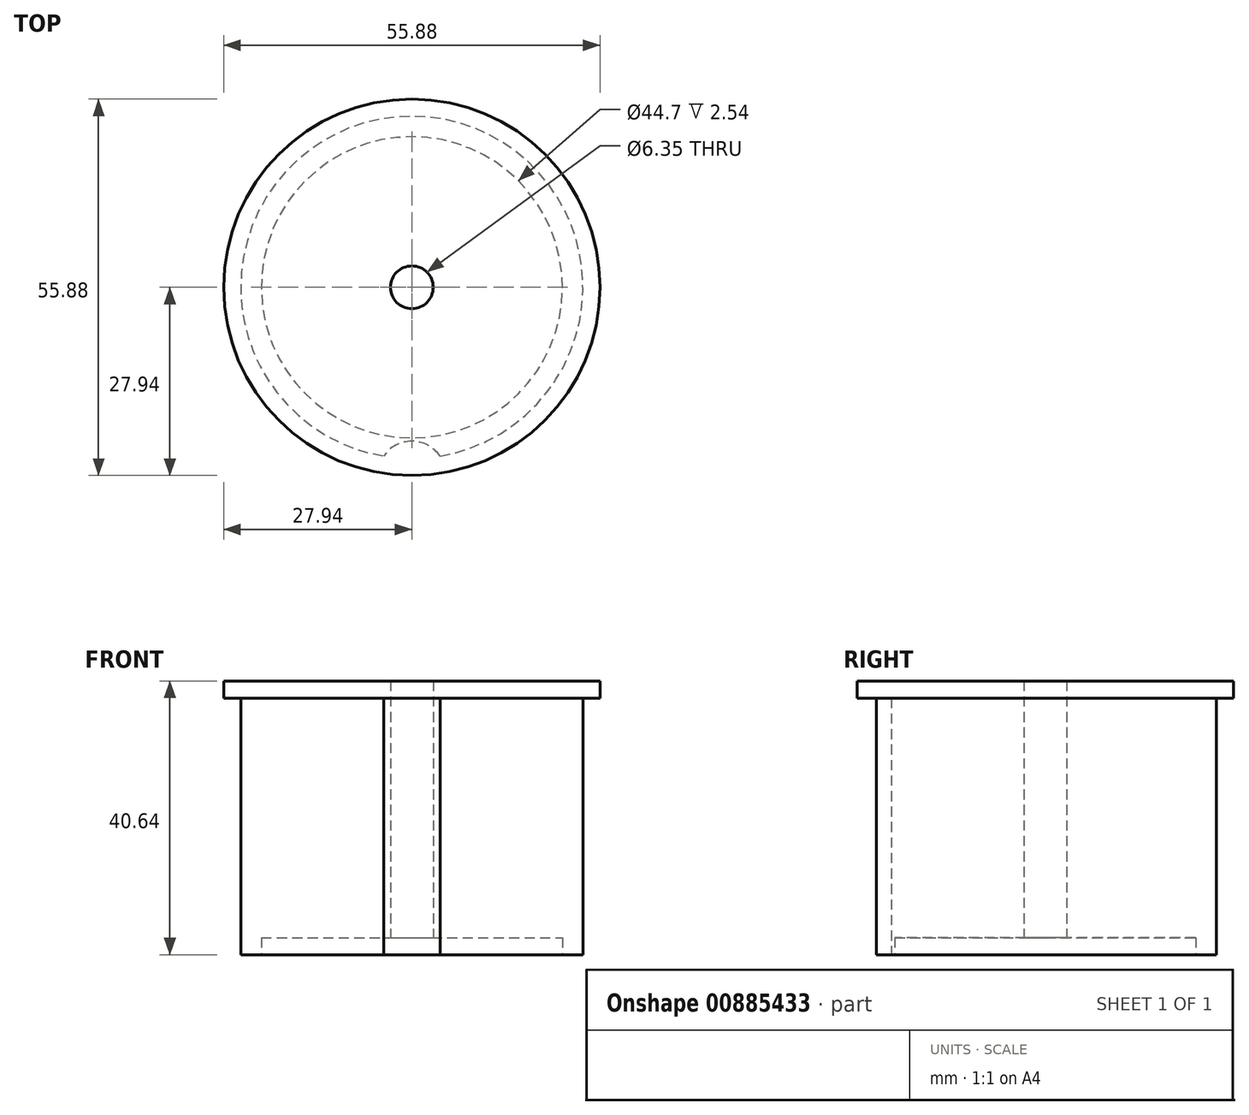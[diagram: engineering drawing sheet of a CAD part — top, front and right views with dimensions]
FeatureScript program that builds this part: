
annotation { "Feature Type Name" : "Feature", "Feature Type Description" : "" }
export const myFeature = defineFeature(function(context is Context, id is Id, definition is map)
    precondition{}
    {
        {
            var Q0;
            Q0=qCreatedBy(makeId("Top.planeOp"),FACE);
            var sketch = newSketch(context, id + "F0", { "sketchPlane" : qUnion([Q0])});
            skCircle(sketch, "E0", {"center": v(0, 0) * mm, "radius": 25.4 * mm});
            skSolve(sketch);
        }
        {
            var Q0;
            Q0 = qSketchRegion(id + "F0", true);
            extrude(context, id + "F1", {"entities" : qUnion([Q0]), "endBound" : BoundingType.SYMMETRIC, "depth" : 38.1 * mm, "offsetDistance" : 25.4 * mm});
        }
        {
            var Q0;
            Q0=makeQuery(id+"F1.opExtrude","CAP_FACE",FACE,{"disambiguationData":[OSD([sQuery(id+"F0.wireOp",EDGE,"E0")])],"isStart":false});
            var sketch = newSketch(context, id + "F2", { "sketchPlane" : qUnion([Q0])});
            skCircle(sketch, "E1", {"center": v(0, 0) * mm, "radius": 27.94 * mm});
            skSolve(sketch);
        }
        {
            var Q0;
            Q0=makeQuery(id+"F2.imprint","IMPRINT",FACE,{"disambiguationData":[TD([[makeQuery(id+"F2.imprint","IMPRINT",EDGE,{"derivedFrom":sQuery(id+"F2.wireOp",EDGE,"E1")}),1.0]])]});
            var Q1;
            Q1=makeQuery(id+"F2.imprint","IMPRINT",FACE,{"disambiguationData":[TD([[makeQuery(id+"F2.imprint","IMPRINT",EDGE,{"derivedFrom":makeQuery(id+"F1.opExtrude","CAP_EDGE",EDGE,{"disambiguationData":[OSD([sQuery(id+"F0.wireOp",EDGE,"E0")])],"isStart":false})}),1.0]])]});
            extrude(context, id + "F3", {"entities" : qUnion([Q0, Q1]), "operationType" : NewBodyOperationType.ADD, "depth" : 2.54 * mm, "offsetDistance" : 25.4 * mm});
        }
        {
            var Q0;
            Q0=makeQuery(id+"F1.opExtrude","CAP_FACE",FACE,{"disambiguationData":[OSD([sQuery(id+"F0.wireOp",EDGE,"E0")])],"isStart":true});
            var sketch = newSketch(context, id + "F4", { "sketchPlane" : qUnion([Q0])});
            skCircle(sketch, "E2", {"center": v(0, 0) * mm, "radius": 22.35 * mm});
            skSolve(sketch);
        }
        {
            var Q0;
            Q0=makeQuery(id+"F4.imprint","IMPRINT",FACE,{"disambiguationData":[TD([[makeQuery(id+"F4.imprint","IMPRINT",EDGE,{"derivedFrom":sQuery(id+"F4.wireOp",EDGE,"E2")}),1.0]])]});
            extrude(context, id + "F5", {"entities" : qUnion([Q0]), "operationType" : NewBodyOperationType.REMOVE, "oppositeDirection" : true, "depth" : 2.54 * mm, "offsetDistance" : 25.4 * mm});
        }
        {
            var Q0;
            Q0=makeQuery(id+"F5.boolean.opBoolean","COPY",FACE,{"derivedFrom":makeQuery(id+"F5.opExtrude","CAP_FACE",FACE,{"disambiguationData":[OSD([sQuery(id+"F4.wireOp",EDGE,"E2")])],"isStart":false})});
            var sketch = newSketch(context, id + "F6", { "sketchPlane" : qUnion([Q0])});
            skCircle(sketch, "E3", {"center": v(0, 0) * mm, "radius": 3.18 * mm});
            skSolve(sketch);
        }
        {
            var Q0;
            Q0=makeQuery(id+"F6.imprint","IMPRINT",FACE,{"disambiguationData":[TD([[makeQuery(id+"F6.imprint","IMPRINT",EDGE,{"derivedFrom":sQuery(id+"F6.wireOp",EDGE,"E3")}),1.0]])]});
            extrude(context, id + "F7", {"entities" : qUnion([Q0]), "operationType" : NewBodyOperationType.REMOVE, "endBound" : BoundingType.THROUGH_ALL, "oppositeDirection" : true, "depth" : 25.4 * mm, "offsetDistance" : 25.4 * mm});
        }
        {
            var Q0;
            Q0=makeQuery(id+"F1.opExtrude","CAP_FACE",FACE,{"disambiguationData":[OSD([sQuery(id+"F0.wireOp",EDGE,"E0")])],"isStart":true});
            var sketch = newSketch(context, id + "F8", { "sketchPlane" : qUnion([Q0])});
            skArc(sketch, "E4", {"start": v(-4.18, 25.05) * mm, "mid": v(0, 22.86) * mm, "end": v(4.18, 25.05) * mm});
            skSolve(sketch);
        }
        {
            var Q0;
            {var subQ0=sQuery(id+"F8.wireOp",EDGE,"E4");Q0=makeQuery(id+"F8.imprint","IMPRINT",FACE,{"disambiguationData":[TD([[makeQuery(id+"F8.imprint","IMPRINT",EDGE,{"derivedFrom":subQ0}),1.0]])]});}
            var Q1;
            Q1=makeQuery(id+"F3.opExtrude","CAP_FACE",FACE,{"disambiguationData":[OSD([sQuery(id+"F2.wireOp",EDGE,"E1")])],"isStart":true});
            extrude(context, id + "F9", {"entities" : qUnion([Q0]), "operationType" : NewBodyOperationType.REMOVE, "endBound" : BoundingType.UP_TO_SURFACE, "oppositeDirection" : true, "depth" : 25.4 * mm, "endBoundEntityFace" : qUnion([Q1]), "offsetDistance" : 25.4 * mm});
        }
    });
